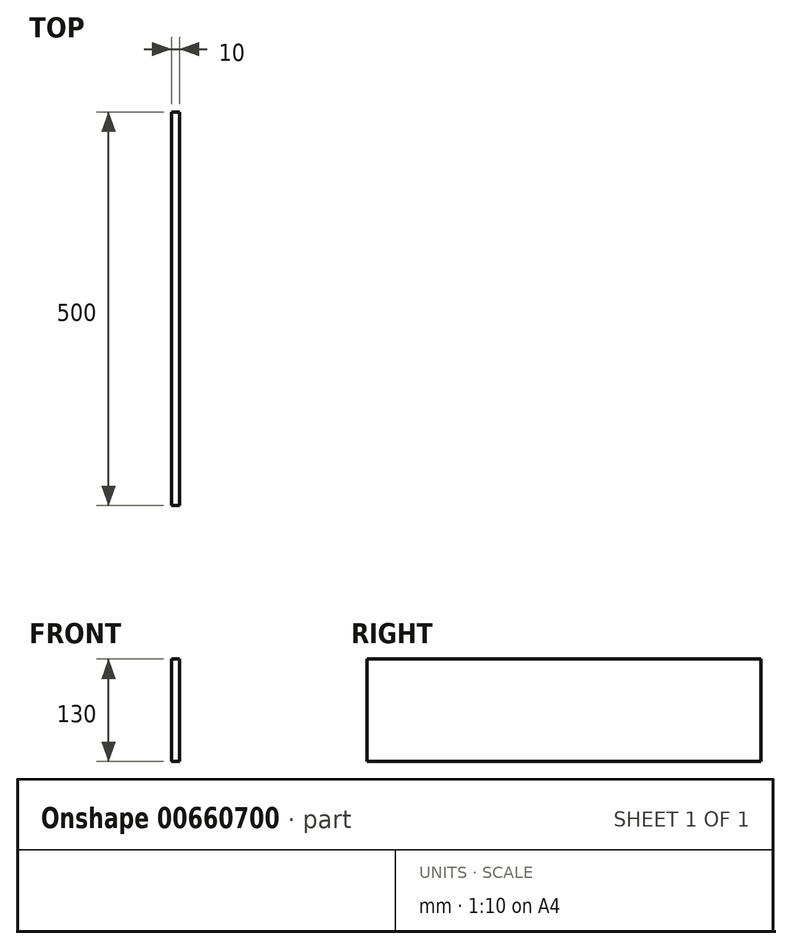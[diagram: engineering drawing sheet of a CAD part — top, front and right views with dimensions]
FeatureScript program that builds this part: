
annotation { "Feature Type Name" : "Feature", "Feature Type Description" : "" }
export const myFeature = defineFeature(function(context is Context, id is Id, definition is map)
    precondition{}
    {
        {
            var Q0;
            Q0=qCreatedBy(makeId("Right.planeOp"),FACE);
            var sketch = newSketch(context, id + "F0", { "sketchPlane" : qUnion([Q0])});
            skLineSegment(sketch, "E0.bottom", {"start": v(0, 0) * mm, "end": v(500, 0) * mm});
            skLineSegment(sketch, "E0.top", {"start": v(0, 130) * mm, "end": v(500, 130) * mm});
            skLineSegment(sketch, "E0.left", {"start": v(0, 0) * mm, "end": v(0, 130) * mm});
            skLineSegment(sketch, "E0.right", {"start": v(500, 0) * mm, "end": v(500, 130) * mm});
            skSolve(sketch);
        }
        {
            var Q0;
            Q0 = qSketchRegion(id + "F0", true);
            extrude(context, id + "F1", {"entities" : qUnion([Q0]), "depth" : 10 * mm, "offsetDistance" : 25 * mm});
        }
    });
